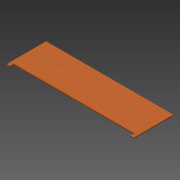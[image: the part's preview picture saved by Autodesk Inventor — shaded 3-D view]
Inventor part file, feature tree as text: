
AUTODESK INVENTOR PART (.ipt)
format: ipt  version: 2013 (Build 170138000, 138)  size: 82,944 bytes
history: native  units: in
note: dims shown in document units (in); Inventor stores cm internally (conversion verified against a paired STEP export)
features: extrude x1, sketch x1
ambient origin geometry x8: Origin, YZ Plane, XZ Plane, XY Plane, X Axis, Y Axis, Z Axis, Center Point
feature tree (2):
  extrude  "Extrusion2"  Depth=18.0in
  sketch  "Sketch1"  dims[d0=58.0in d1=18.0in d4=1.75in d8=0.5in d9=0.0in d10=1.5in d11=1.5in]
